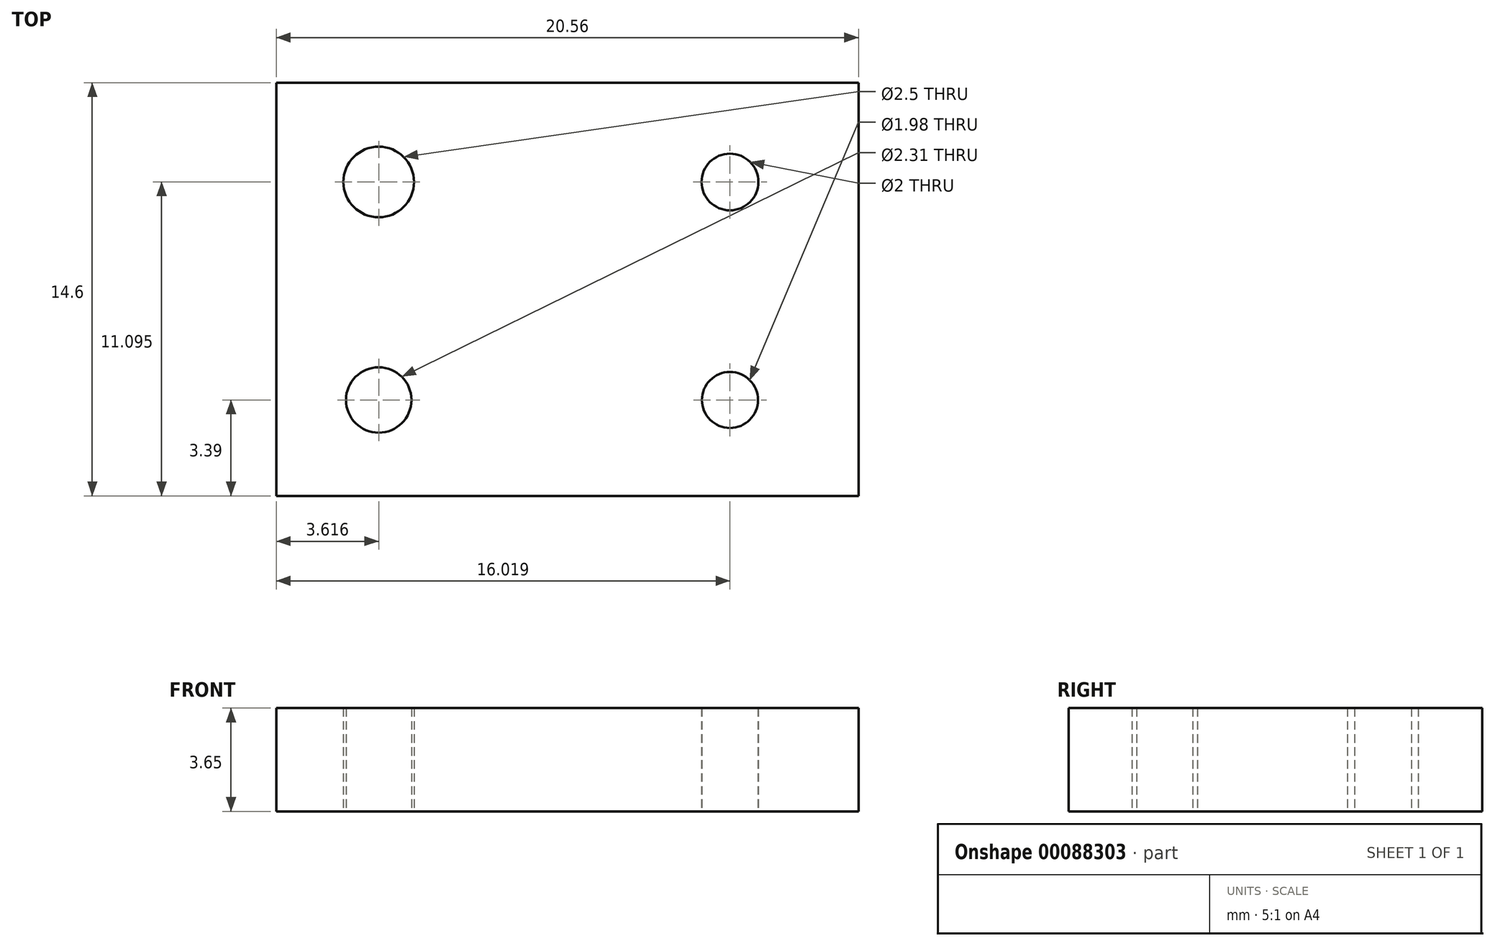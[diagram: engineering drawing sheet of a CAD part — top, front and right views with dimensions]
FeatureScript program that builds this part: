
annotation { "Feature Type Name" : "Feature", "Feature Type Description" : "" }
export const myFeature = defineFeature(function(context is Context, id is Id, definition is map)
    precondition{}
    {
        {
            var Q0;
            Q0=qCreatedBy(makeId("Top.planeOp"),FACE);
            var sketch = newSketch(context, id + "F0", { "sketchPlane" : qUnion([Q0])});
            skLineSegment(sketch, "E0.bottom", {"start": v(-61.68, 39.78) * mm, "end": v(-41.12, 39.78) * mm});
            skLineSegment(sketch, "E0.top", {"start": v(-61.68, 25.18) * mm, "end": v(-41.12, 25.18) * mm});
            skLineSegment(sketch, "E0.left", {"start": v(-61.68, 39.78) * mm, "end": v(-61.68, 25.18) * mm});
            skLineSegment(sketch, "E0.right", {"start": v(-41.12, 39.78) * mm, "end": v(-41.12, 25.18) * mm});
            skSolve(sketch);
        }
        {
            var Q0;
            Q0 = qSketchRegion(id + "F0", true);
            extrude(context, id + "F1", {"entities" : qUnion([Q0]), "depth" : 3.65 * mm});
        }
        {
            var Q0;
            Q0=qCreatedBy(makeId("Top.planeOp"),FACE);
            var sketch = newSketch(context, id + "F2", { "sketchPlane" : qUnion([Q0])});
            skCircle(sketch, "E1", {"center": v(-58.06, 36.27) * mm, "radius": 1.25 * mm});
            skCircle(sketch, "E2", {"center": v(-45.66, 36.27) * mm, "radius": 1 * mm});
            skCircle(sketch, "E3", {"center": v(-58.06, 28.57) * mm, "radius": 1.16 * mm});
            skCircle(sketch, "E4", {"center": v(-45.66, 28.57) * mm, "radius": 1 * mm});
            skSolve(sketch);
        }
        {
            var Q0;
            Q0 = qSketchRegion(id + "F2", true);
            extrude(context, id + "F3", {"entities" : qUnion([Q0]), "operationType" : NewBodyOperationType.REMOVE, "depth" : 25.4 * mm});
        }
    });
